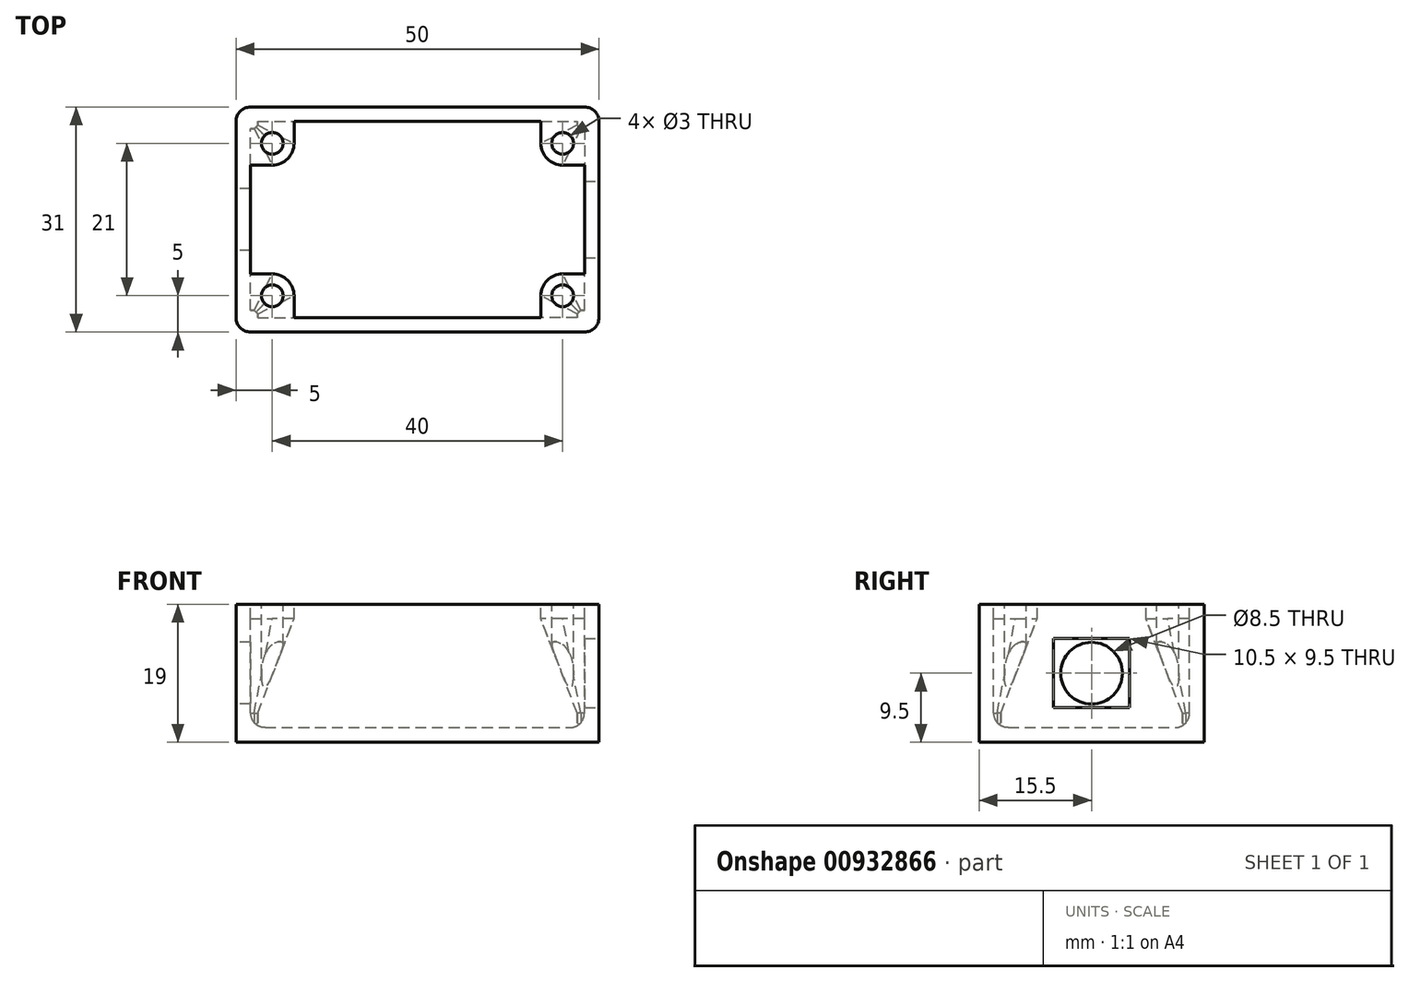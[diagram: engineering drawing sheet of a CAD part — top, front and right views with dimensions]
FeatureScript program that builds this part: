
annotation { "Feature Type Name" : "Feature", "Feature Type Description" : "" }
export const myFeature = defineFeature(function(context is Context, id is Id, definition is map)
    precondition{}
    {
        {
            var Q0;
            Q0=qCreatedBy(makeId("Top.planeOp"),FACE);
            var sketch = newSketch(context, id + "F0", { "sketchPlane" : qUnion([Q0])});
            skLineSegment(sketch, "E0.bottom", {"start": v(0, 0) * mm, "end": v(50, 0) * mm});
            skLineSegment(sketch, "E0.top", {"start": v(0, 31) * mm, "end": v(50, 31) * mm});
            skLineSegment(sketch, "E0.left", {"start": v(0, 0) * mm, "end": v(0, 31) * mm});
            skLineSegment(sketch, "E0.right", {"start": v(50, 0) * mm, "end": v(50, 31) * mm});
            skSolve(sketch);
        }
        {
            var Q0;
            Q0 = qSketchRegion(id + "F0", true);
            extrude(context, id + "F1", {"entities" : qUnion([Q0]), "depth" : 19 * mm, "offsetDistance" : 25 * mm});
        }
        {
            var Q0;
            Q0=makeQuery(id+"F1.opExtrude","CAP_FACE",FACE,{"disambiguationData":[OSD([sQuery(id+"F0.wireOp",EDGE,"E0.bottom"),sQuery(id+"F0.wireOp",EDGE,"E0.top"),sQuery(id+"F0.wireOp",EDGE,"E0.left"),sQuery(id+"F0.wireOp",EDGE,"E0.right")])],"isStart":false});
            shell(context, id + "F2", {"entities" : qUnion([Q0]), "thickness" : 2 * mm});
        }
        {
            var Q0;
            Q0=makeQuery(id+"F1.opExtrude","SWEPT_FACE",FACE,{"disambiguationData":[OSD([sQuery(id+"F0.wireOp",EDGE,"E0.right")])]});
            var sketch = newSketch(context, id + "F3", { "sketchPlane" : qUnion([Q0])});
            skLineSegment(sketch, "E1", {"start": v(0, 0) * mm, "end": v(31, 19) * mm, "construction": true});
            skLineSegment(sketch, "E2", {"start": v(0, 19) * mm, "end": v(31, 0) * mm, "construction": true});
            skPoint(sketch, "E3", {"position": v(15.5, 9.5) * mm});
            skLineSegment(sketch, "E4.bottom", {"start": v(20.75, 14.25) * mm, "end": v(10.25, 14.25) * mm});
            skLineSegment(sketch, "E4.top", {"start": v(20.75, 4.75) * mm, "end": v(10.25, 4.75) * mm});
            skLineSegment(sketch, "E4.left", {"start": v(20.75, 14.25) * mm, "end": v(20.75, 4.75) * mm});
            skLineSegment(sketch, "E4.right", {"start": v(10.25, 14.25) * mm, "end": v(10.25, 4.75) * mm});
            skSolve(sketch);
        }
        {
            var Q0;
            Q0=makeQuery(id+"F3.imprint","IMPRINT",FACE,{"disambiguationData":[TD([[makeQuery(id+"F3.imprint","IMPRINT",EDGE,{"derivedFrom":sQuery(id+"F3.wireOp",EDGE,"E4.bottom")}),1.0]])]});
            var Q1;
            Q1=makeQuery(id+"F2.opShell","OFFSET_FACE",FACE,{"disambiguationData":[OSD([sQuery(id+"F0.wireOp",EDGE,"E0.right")])]});
            extrude(context, id + "F4", {"entities" : qUnion([Q0]), "operationType" : NewBodyOperationType.REMOVE, "endBound" : BoundingType.UP_TO_SURFACE, "oppositeDirection" : true, "depth" : 3 * mm, "endBoundEntityFace" : qUnion([Q1]), "offsetDistance" : 25 * mm});
        }
        {
            var Q0;
            Q0=makeQuery(id+"F1.opExtrude","SWEPT_FACE",FACE,{"disambiguationData":[OSD([sQuery(id+"F0.wireOp",EDGE,"E0.left")])]});
            var sketch = newSketch(context, id + "F5", { "sketchPlane" : qUnion([Q0])});
            skCircle(sketch, "E5", {"center": v(-15.5, 9.5) * mm, "radius": 4.25 * mm});
            skSolve(sketch);
        }
        {
            var Q0;
            Q0=makeQuery(id+"F5.imprint","IMPRINT",FACE,{"disambiguationData":[TD([[makeQuery(id+"F5.imprint","IMPRINT",EDGE,{"derivedFrom":sQuery(id+"F5.wireOp",EDGE,"E5")}),1.0]])]});
            extrude(context, id + "F6", {"entities" : qUnion([Q0]), "operationType" : NewBodyOperationType.REMOVE, "oppositeDirection" : true, "depth" : 2 * mm, "offsetDistance" : 25 * mm});
        }
        {
            var Q0;
            Q0=makeQuery(id+"F1.opExtrude","CAP_FACE",FACE,{"disambiguationData":[OSD([sQuery(id+"F0.wireOp",EDGE,"E0.bottom"),sQuery(id+"F0.wireOp",EDGE,"E0.top"),sQuery(id+"F0.wireOp",EDGE,"E0.left"),sQuery(id+"F0.wireOp",EDGE,"E0.right")])],"isStart":false});
            var sketch = newSketch(context, id + "F7", { "sketchPlane" : qUnion([Q0])});
            skArc(sketch, "E6", {"start": v(42, 26) * mm, "mid": v(42.88, 23.88) * mm, "end": v(45, 23) * mm});
            skLineSegment(sketch, "E7.bottom", {"start": v(48, 29) * mm, "end": v(42, 29) * mm});
            skLineSegment(sketch, "E7.top", {"start": v(48, 23) * mm, "end": v(45, 23) * mm});
            skLineSegment(sketch, "E7.left", {"start": v(48, 29) * mm, "end": v(48, 23) * mm});
            skLineSegment(sketch, "E7.right", {"start": v(42, 29) * mm, "end": v(42, 26) * mm});
            skPoint(sketch, "E8.orphan", {"position": v(42, 23) * mm});
            skLineSegment(sketch, "E9", {"start": v(2, 15.5) * mm, "end": v(48, 15.5) * mm, "construction": true});
            skLineSegment(sketch, "E10", {"start": v(25, 2) * mm, "end": v(25, 29) * mm, "construction": true});
            skLineSegment(sketch, "E11.MirrorCS", {"start": v(2, 29) * mm, "end": v(8, 29) * mm});
            skLineSegment(sketch, "E12.MirrorCS", {"start": v(8, 29) * mm, "end": v(8, 26) * mm});
            skArc(sketch, "E13.MirrorCS", {"start": v(8, 26) * mm, "mid": v(7.12, 23.88) * mm, "end": v(5, 23) * mm});
            skLineSegment(sketch, "E14.MirrorCS", {"start": v(2, 23) * mm, "end": v(5, 23) * mm});
            skLineSegment(sketch, "E15.MirrorCS", {"start": v(2, 29) * mm, "end": v(2, 23) * mm});
            skLineSegment(sketch, "E16.MirrorCS", {"start": v(2, 2) * mm, "end": v(2, 8) * mm});
            skLineSegment(sketch, "E17.MirrorCS", {"start": v(2, 8) * mm, "end": v(5, 8) * mm});
            skArc(sketch, "E18.MirrorCS", {"start": v(8, 5) * mm, "mid": v(7.12, 7.12) * mm, "end": v(5, 8) * mm});
            skLineSegment(sketch, "E19.MirrorCS", {"start": v(8, 2) * mm, "end": v(8, 5) * mm});
            skLineSegment(sketch, "E20.MirrorCS", {"start": v(2, 2) * mm, "end": v(8, 2) * mm});
            skLineSegment(sketch, "E21.MirrorCS", {"start": v(48, 2) * mm, "end": v(42, 2) * mm});
            skLineSegment(sketch, "E22.MirrorCS", {"start": v(42, 2) * mm, "end": v(42, 5) * mm});
            skArc(sketch, "E23.MirrorCS", {"start": v(42, 5) * mm, "mid": v(42.88, 7.12) * mm, "end": v(45, 8) * mm});
            skLineSegment(sketch, "E24.MirrorCS", {"start": v(48, 8) * mm, "end": v(45, 8) * mm});
            skLineSegment(sketch, "E25.MirrorCS", {"start": v(48, 2) * mm, "end": v(48, 8) * mm});
            skSolve(sketch);
        }
        {
            var Q0;
            Q0=makeQuery(id+"F2.opShell","OFFSET_FACE",FACE,{"disambiguationData":[OSD([sQuery(id+"F0.wireOp",EDGE,"E0.bottom"),sQuery(id+"F0.wireOp",EDGE,"E0.top"),sQuery(id+"F0.wireOp",EDGE,"E0.left"),sQuery(id+"F0.wireOp",EDGE,"E0.right")])]});
            var sketch = newSketch(context, id + "F8", { "sketchPlane" : qUnion([Q0])});
            skPoint(sketch, "E26", {"position": v(2, 2) * mm});
            skLineSegment(sketch, "E27.bottom", {"start": v(2, 2) * mm, "end": v(3, 2) * mm});
            skLineSegment(sketch, "E27.top", {"start": v(2, 3) * mm, "end": v(2.5, 3) * mm});
            skLineSegment(sketch, "E27.left", {"start": v(2, 2) * mm, "end": v(2, 3) * mm});
            skLineSegment(sketch, "E27.right", {"start": v(3, 2) * mm, "end": v(3, 2.5) * mm});
            skLineSegment(sketch, "E28", {"start": v(2.5, 3) * mm, "end": v(3, 2.5) * mm});
            skPoint(sketch, "E29.orphan", {"position": v(3, 3) * mm});
            skPoint(sketch, "E30.MirrorCS.end.orphan", {"position": v(2.5, 28) * mm});
            skPoint(sketch, "E31.MirrorCS.end.orphan", {"position": v(3, 28.5) * mm});
            skPoint(sketch, "E32.start.orphan", {"position": v(3, 29) * mm});
            skPoint(sketch, "E33.end.orphan", {"position": v(2, 28) * mm});
            skLineSegment(sketch, "E34", {"start": v(25, 29) * mm, "end": v(25, 2) * mm, "construction": true});
            skLineSegment(sketch, "E35", {"start": v(2, 15.5) * mm, "end": v(48, 15.5) * mm, "construction": true});
            skLineSegment(sketch, "E36.MirrorCS", {"start": v(2, 29) * mm, "end": v(2, 28) * mm});
            skLineSegment(sketch, "E37.MirrorCS", {"start": v(2, 29) * mm, "end": v(3, 29) * mm});
            skLineSegment(sketch, "E38.MirrorCS", {"start": v(3, 29) * mm, "end": v(3, 28.5) * mm});
            skLineSegment(sketch, "E39.MirrorCS", {"start": v(2.5, 28) * mm, "end": v(3, 28.5) * mm});
            skLineSegment(sketch, "E40", {"start": v(2, 28) * mm, "end": v(2.5, 28) * mm});
            skLineSegment(sketch, "E41.MirrorCS", {"start": v(48, 2) * mm, "end": v(47, 2) * mm});
            skLineSegment(sketch, "E42.MirrorCS", {"start": v(47, 2) * mm, "end": v(47, 2.5) * mm});
            skLineSegment(sketch, "E43.MirrorCS", {"start": v(47.5, 3) * mm, "end": v(47, 2.5) * mm});
            skLineSegment(sketch, "E44.MirrorCS", {"start": v(48, 3) * mm, "end": v(47.5, 3) * mm});
            skLineSegment(sketch, "E45.MirrorCS", {"start": v(48, 2) * mm, "end": v(48, 3) * mm});
            skLineSegment(sketch, "E46.MirrorCS", {"start": v(48, 28) * mm, "end": v(47.5, 28) * mm});
            skLineSegment(sketch, "E47.MirrorCS", {"start": v(47.5, 28) * mm, "end": v(47, 28.5) * mm});
            skLineSegment(sketch, "E48.MirrorCS", {"start": v(47, 29) * mm, "end": v(47, 28.5) * mm});
            skLineSegment(sketch, "E49.MirrorCS", {"start": v(48, 29) * mm, "end": v(47, 29) * mm});
            skLineSegment(sketch, "E50.MirrorCS", {"start": v(48, 29) * mm, "end": v(48, 28) * mm});
            skSolve(sketch);
        }
        {
            var Q0;
            Q0=makeQuery(id+"F7.imprint","IMPRINT",FACE,{"disambiguationData":[TD([[makeQuery(id+"F7.imprint","IMPRINT",EDGE,{"derivedFrom":sQuery(id+"F7.wireOp",EDGE,"E21.MirrorCS")}),1.0]])]});
            var Q1;
            Q1=makeQuery(id+"F7.imprint","IMPRINT",FACE,{"disambiguationData":[TD([[makeQuery(id+"F7.imprint","IMPRINT",EDGE,{"derivedFrom":sQuery(id+"F7.wireOp",EDGE,"E16.MirrorCS")}),-1.0]])]});
            var Q2;
            Q2=makeQuery(id+"F7.imprint","IMPRINT",FACE,{"disambiguationData":[TD([[makeQuery(id+"F7.imprint","IMPRINT",EDGE,{"derivedFrom":sQuery(id+"F7.wireOp",EDGE,"E11.MirrorCS")}),-1.0]])]});
            var Q3;
            Q3=makeQuery(id+"F7.imprint","IMPRINT",FACE,{"disambiguationData":[TD([[makeQuery(id+"F7.imprint","IMPRINT",EDGE,{"derivedFrom":sQuery(id+"F7.wireOp",EDGE,"E6")}),1.0]])]});
            extrude(context, id + "F9", {"entities" : qUnion([Q0, Q1, Q2, Q3]), "operationType" : NewBodyOperationType.ADD, "oppositeDirection" : true, "depth" : 2 * mm, "offsetDistance" : 25 * mm});
        }
        {
            var Q0;
            Q0=makeQuery(id+"F8.imprint","IMPRINT",FACE,{"disambiguationData":[TD([[makeQuery(id+"F8.imprint","IMPRINT",EDGE,{"derivedFrom":sQuery(id+"F8.wireOp",EDGE,"E27.bottom")}),1.0]])]});
            var Q1;
            Q1=makeQuery(id+"F8.imprint","IMPRINT",FACE,{"disambiguationData":[TD([[makeQuery(id+"F8.imprint","IMPRINT",EDGE,{"derivedFrom":sQuery(id+"F8.wireOp",EDGE,"E46.MirrorCS")}),-1.0]])]});
            var Q2;
            Q2=makeQuery(id+"F8.imprint","IMPRINT",FACE,{"disambiguationData":[TD([[makeQuery(id+"F8.imprint","IMPRINT",EDGE,{"derivedFrom":sQuery(id+"F8.wireOp",EDGE,"E41.MirrorCS")}),1.0]])]});
            var Q3;
            Q3 = qSketchRegion(id + "F8", true);
            var Q4;
            Q4=makeQuery(id+"F8.imprint","IMPRINT",FACE,{"disambiguationData":[TD([[makeQuery(id+"F8.imprint","IMPRINT",EDGE,{"derivedFrom":sQuery(id+"F8.wireOp",EDGE,"E36.MirrorCS")}),-1.0]])]});
            extrude(context, id + "F10", {"entities" : qUnion([Q0, Q1, Q2, Q3, Q4]), "operationType" : NewBodyOperationType.ADD, "depth" : 2 * mm, "offsetDistance" : 25 * mm});
        }
        {
            var Q1;
            Q1=makeQuery(id+"F10.opExtrude","CAP_FACE",FACE,{"disambiguationData":[OSD([sQuery(id+"F8.wireOp",EDGE,"E27.bottom"),sQuery(id+"F8.wireOp",EDGE,"E27.top"),sQuery(id+"F8.wireOp",EDGE,"E27.left"),sQuery(id+"F8.wireOp",EDGE,"E27.right"),sQuery(id+"F8.wireOp",EDGE,"E28")])],"isStart":false});
            var Q2;
            Q2=makeQuery(id+"F9.opExtrude","CAP_FACE",FACE,{"disambiguationData":[OSD([sQuery(id+"F7.wireOp",EDGE,"E16.MirrorCS"),sQuery(id+"F7.wireOp",EDGE,"E17.MirrorCS"),sQuery(id+"F7.wireOp",EDGE,"E18.MirrorCS"),sQuery(id+"F7.wireOp",EDGE,"E19.MirrorCS"),sQuery(id+"F7.wireOp",EDGE,"E20.MirrorCS")])],"isStart":false});
            loft(context, id + "F11", {"operationType" : NewBodyOperationType.ADD, "sheetProfilesArray" : [{ "sheetProfileEntities" : qUnion([Q1]) }, { "sheetProfileEntities" : qUnion([Q2]) }]});
        }
        {
            var Q1;
            Q1=makeQuery(id+"F10.opExtrude","CAP_FACE",FACE,{"disambiguationData":[OSD([sQuery(id+"F8.wireOp",EDGE,"E41.MirrorCS"),sQuery(id+"F8.wireOp",EDGE,"E42.MirrorCS"),sQuery(id+"F8.wireOp",EDGE,"E43.MirrorCS"),sQuery(id+"F8.wireOp",EDGE,"E44.MirrorCS"),sQuery(id+"F8.wireOp",EDGE,"E45.MirrorCS")])],"isStart":false});
            var Q2;
            Q2=makeQuery(id+"F9.opExtrude","CAP_FACE",FACE,{"disambiguationData":[OSD([sQuery(id+"F7.wireOp",EDGE,"E21.MirrorCS"),sQuery(id+"F7.wireOp",EDGE,"E22.MirrorCS"),sQuery(id+"F7.wireOp",EDGE,"E23.MirrorCS"),sQuery(id+"F7.wireOp",EDGE,"E24.MirrorCS"),sQuery(id+"F7.wireOp",EDGE,"E25.MirrorCS")])],"isStart":false});
            loft(context, id + "F12", {"operationType" : NewBodyOperationType.ADD, "sheetProfilesArray" : [{ "sheetProfileEntities" : qUnion([Q1]) }, { "sheetProfileEntities" : qUnion([Q2]) }]});
        }
        {
            var Q1;
            Q1=makeQuery(id+"F10.opExtrude","CAP_FACE",FACE,{"disambiguationData":[OSD([sQuery(id+"F8.wireOp",EDGE,"E36.MirrorCS"),sQuery(id+"F8.wireOp",EDGE,"E37.MirrorCS"),sQuery(id+"F8.wireOp",EDGE,"E38.MirrorCS"),sQuery(id+"F8.wireOp",EDGE,"E39.MirrorCS"),sQuery(id+"F8.wireOp",EDGE,"E40")])],"isStart":false});
            var Q2;
            Q2=makeQuery(id+"F9.opExtrude","CAP_FACE",FACE,{"disambiguationData":[OSD([sQuery(id+"F7.wireOp",EDGE,"E11.MirrorCS"),sQuery(id+"F7.wireOp",EDGE,"E12.MirrorCS"),sQuery(id+"F7.wireOp",EDGE,"E13.MirrorCS"),sQuery(id+"F7.wireOp",EDGE,"E14.MirrorCS"),sQuery(id+"F7.wireOp",EDGE,"E15.MirrorCS")])],"isStart":false});
            loft(context, id + "F13", {"operationType" : NewBodyOperationType.ADD, "sheetProfilesArray" : [{ "sheetProfileEntities" : qUnion([Q1]) }, { "sheetProfileEntities" : qUnion([Q2]) }]});
        }
        {
            var Q1;
            Q1=makeQuery(id+"F10.opExtrude","CAP_FACE",FACE,{"disambiguationData":[OSD([sQuery(id+"F8.wireOp",EDGE,"E46.MirrorCS"),sQuery(id+"F8.wireOp",EDGE,"E47.MirrorCS"),sQuery(id+"F8.wireOp",EDGE,"E48.MirrorCS"),sQuery(id+"F8.wireOp",EDGE,"E49.MirrorCS"),sQuery(id+"F8.wireOp",EDGE,"E50.MirrorCS")])],"isStart":false});
            var Q2;
            Q2=makeQuery(id+"F9.opExtrude","CAP_FACE",FACE,{"disambiguationData":[OSD([sQuery(id+"F7.wireOp",EDGE,"E6"),sQuery(id+"F7.wireOp",EDGE,"E7.bottom"),sQuery(id+"F7.wireOp",EDGE,"E7.top"),sQuery(id+"F7.wireOp",EDGE,"E7.left"),sQuery(id+"F7.wireOp",EDGE,"E7.right")])],"isStart":false});
            loft(context, id + "F14", {"operationType" : NewBodyOperationType.ADD, "sheetProfilesArray" : [{ "sheetProfileEntities" : qUnion([Q1]) }, { "sheetProfileEntities" : qUnion([Q2]) }]});
        }
        {
            var Q0;
            Q0=sQuery(id+"F7.wireOp",VERTEX,"E23.MirrorCS.center");
            var Q1;
            Q1=sQuery(id+"F7.wireOp",VERTEX,"E6.center");
            var Q2;
            Q2=sQuery(id+"F7.wireOp",VERTEX,"E13.MirrorCS.center");
            var Q3;
            Q3=sQuery(id+"F7.wireOp",VERTEX,"E18.MirrorCS.center");
            var Q4;
            Q4=makeQuery(id+"F1.opExtrude","SWEPT_BODY",BODY,{"disambiguationData":[OSD([sQuery(id+"F0.wireOp",EDGE,"E0.bottom"),sQuery(id+"F0.wireOp",EDGE,"E0.top"),sQuery(id+"F0.wireOp",EDGE,"E0.left"),sQuery(id+"F0.wireOp",EDGE,"E0.right")])]});
            hole(context, id + "F15", {"style" : HoleStyle.SIMPLE, "endStyle" : HoleEndStyle.BLIND, "holeDiameter" : 3 * mm, "majorDiameter" : 5 * mm, "holeDepth" : 12 * mm, "isTappedThrough" : true, "tappedDepth" : 12 * mm, "tapClearance" : 3, "locations" : qUnion([Q0, Q1, Q2, Q3]), "scope" : qUnion([Q4])});
        }
        {
            var Q0;
            Q0=makeQuery(id+"F1.opExtrude","SWEPT_EDGE",EDGE,{"disambiguationData":[OSD([sQuery(id+"F0.wireOp",EDGE,"E0.bottom"),sQuery(id+"F0.wireOp",EDGE,"E0.right")])]});
            var Q1;
            Q1=makeQuery(id+"F1.opExtrude","SWEPT_EDGE",EDGE,{"disambiguationData":[OSD([sQuery(id+"F0.wireOp",EDGE,"E0.bottom"),sQuery(id+"F0.wireOp",EDGE,"E0.left")])]});
            var Q2;
            Q2=makeQuery(id+"F1.opExtrude","SWEPT_EDGE",EDGE,{"disambiguationData":[OSD([sQuery(id+"F0.wireOp",EDGE,"E0.top"),sQuery(id+"F0.wireOp",EDGE,"E0.right")])]});
            var Q3;
            Q3=makeQuery(id+"F1.opExtrude","SWEPT_EDGE",EDGE,{"disambiguationData":[OSD([sQuery(id+"F0.wireOp",EDGE,"E0.top"),sQuery(id+"F0.wireOp",EDGE,"E0.left")])]});
            fillet(context, id + "F16", {"entities" : qUnion([Q0, Q1, Q2, Q3]), "radius" : 2 * mm, "tangentPropagation" : true, "allowEdgeOverflow" : false});
        }
        {
            var Q0;
            {var subQ0=sQuery(id+"F0.wireOp",EDGE,"E0.bottom");Q0=makeQuery(id+"F2.opShell","OFFSET_EDGE",EDGE,{"disambiguationData":[OSD([subQ0]),TDD([makeQuery(id+"F1.opExtrude","CAP_EDGE",EDGE,{"disambiguationData":[OSD([subQ0])],"isStart":true})])]});}
            var Q1;
            {var subQ0=sQuery(id+"F0.wireOp",EDGE,"E0.right");Q1=makeQuery(id+"F2.opShell","OFFSET_EDGE",EDGE,{"disambiguationData":[OSD([subQ0]),TDD([makeQuery(id+"F1.opExtrude","CAP_EDGE",EDGE,{"disambiguationData":[OSD([subQ0])],"isStart":true})])]});}
            var Q2;
            {var subQ0=sQuery(id+"F0.wireOp",EDGE,"E0.top");Q2=makeQuery(id+"F2.opShell","OFFSET_EDGE",EDGE,{"disambiguationData":[OSD([subQ0]),TDD([makeQuery(id+"F1.opExtrude","CAP_EDGE",EDGE,{"disambiguationData":[OSD([subQ0])],"isStart":true})])]});}
            var Q3;
            {var subQ0=sQuery(id+"F0.wireOp",EDGE,"E0.left");Q3=makeQuery(id+"F2.opShell","OFFSET_EDGE",EDGE,{"disambiguationData":[OSD([subQ0]),TDD([makeQuery(id+"F1.opExtrude","CAP_EDGE",EDGE,{"disambiguationData":[OSD([subQ0])],"isStart":true})])]});}
            fillet(context, id + "F17", {"entities" : qUnion([Q0, Q1, Q2, Q3]), "radius" : 2 * mm, "tangentPropagation" : true, "allowEdgeOverflow" : false});
        }
    });
